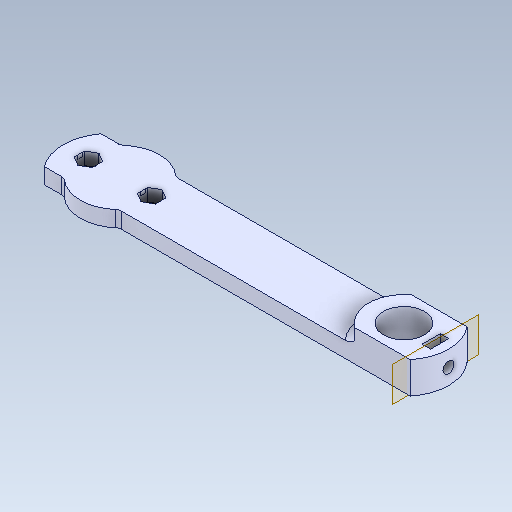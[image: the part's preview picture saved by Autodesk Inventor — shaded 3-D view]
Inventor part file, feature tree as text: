
AUTODESK INVENTOR PART (.ipt)
format: ipt  version: 2021 (Build 250183000, 183)  size: 408,576 bytes
history: native  units: in
note: dims shown in document units (in); Inventor stores cm internally (conversion verified against a paired STEP export)
features: sketch x20, extrude x17, fillet x3, projected_geometry x2, delete_face x1, chamfer x1, hole x1, plane x1, other x1
ambient origin geometry x8: Origin, YZ Plane, XZ Plane, XY Plane, X Axis, Y Axis, Z Axis, Center Point
bodies: Solid1 (feature_tree)
feature tree (47):
  extrude  "Extrusion1"  Depth=0.3937in TaperAngle=0.0deg
  extrude  "Extrusion2"  TaperAngle=0.0deg  [1 undecoded]
  sketch  "Sketch5"  dims[d9=0.3937in d10=0.0in d11=0.878in d12=0.3937in d13=0.0in]
  delete_face  "Delete Face1"
  extrude  "Extrusion4"  Depth=0.9843in
  extrude  "Extrusion5"  Depth=0.878in
  chamfer  "Chamfer1"  Distance=0.3937in
  sketch  "Sketch8"  dims[d32=0.3937in d33=0.0in d34=0.0787in d35=0.0787in d36=0.0in]
  extrude  "Extrusion7"  Depth=0.0787in
  extrude  "Extrusion9"  Depth=3.5433in
  extrude  "Extrusion8"  Depth=0.0787in
  fillet  "Fillet2"  Radius=0.0787in
  hole  "Hole1"  [1 undecoded]
  extrude  "Extrusion10"  Depth=0.0787in
  extrude  "Extrusion11"  Depth=0.0787in
  extrude  "Extrusion12"  Depth=0.1378in
  fillet  "Fillet3"  Radius=0.3937in
  extrude  "Extrusion3"  Depth=0.0118in
  extrude  "Extrusion13"  Depth=0.0394in
  extrude  "Extrusion14"  TaperAngle=0.0deg  [1 undecoded]
  extrude  "Extrusion15"  Depth=0.5906in
  extrude  "Extrusion16"  Depth=0.3937in TaperAngle=0.0deg
  plane  "Work Plane1"
  extrude  "Extrusion17"  Depth=0.3937in TaperAngle=0.0deg
  extrude  "Extrusion18"  Depth=0.3937in
  fillet  "Fillet4"  Radius=0.1969in
  sketch  "Sketch1"  dims[d0=0.7874in d1=0.3937in d2=0.0in]
  sketch  "Sketch2"  dims[d3=0.3937in d4=0.0in d5=0.0in]
  sketch  "Sketch4"  dims[d6=0.3937in d7=0.0in d8=0.9843in]
  sketch  "Sketch6"  dims[d14=0.0197in d15=0.0787in d16=45.0deg d28=0.7087in]
  sketch  "Sketch7"  dims[d29=0.3937in d30=0.0in d31=3.5433in]
  sketch  "Sketch11"  dims[d37=0.7874in d39=0.4921in]
  sketch  "Sketch12"  dims[d40=0.1378in d41=0.2362in d42=0.1575in d43=0.0787in d44=90.0deg d45=0.315in d46=0.8108in d47=0.2264in]
  sketch  "Sketch13"  dims[d48=0.0787in d49=0.0in d50=1.1811in]
  sketch  "Sketch14"  dims[d52=0.1181in d53=0.1378in d54=0.3937in d55=0.0in]
  projected_geometry  "Projected Loop3"
  projected_geometry  "Projected Loop4"
  sketch  "Sketch15"  dims[d56=0.0472in d57=0.0118in]
  sketch  "Sketch16"  dims[d60=0.0591in d61=0.0in d62=0.0394in]
  sketch  "Sketch17"  dims[d63=0.5118in d64=0.0in d65=0.0in]
  sketch  "Sketch18"  dims[d66=0.2362in d67=0.5906in]
  sketch  "Sketch19"  dims[d68=0.9843in d69=0.3937in d70=0.0in]
  sketch  "Sketch20"  dims[d71=1.1811in d72=0.3937in d73=0.0in]
  sketch  "Sketch21"  dims[d74=0.3937in d75=0.0in d76=0.3937in d77=0.1969in]
  sketch  "Sketch22"  dims[d78=0.1378in]
  sketch  "Sketch23"  dims[d79=0.5906in d80=0.0in d81=0.4331in d82=0.2283in d83=0.1063in d84=0.0in d85=0.0787in]
  other  "Cut-Extrude3"
note: 3 required parameter values undecoded (feature->parameter linkage not recoverable at this tier; creation-order binding heuristic only, values carry confidence <= 0.55)
